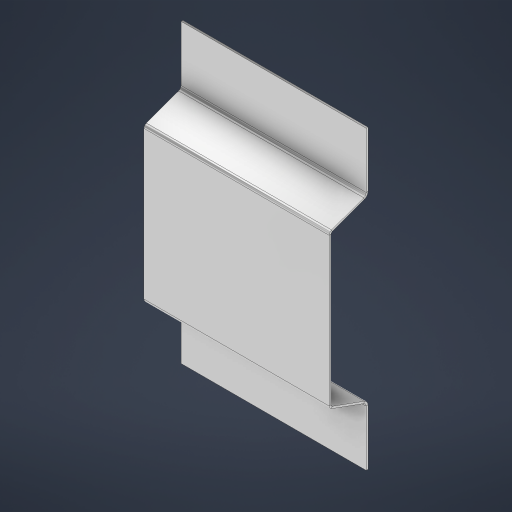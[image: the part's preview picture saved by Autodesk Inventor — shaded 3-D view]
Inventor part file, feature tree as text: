
AUTODESK INVENTOR PART (.ipt)
format: ipt  version: 2024.3 (Build 283343010, 343A)  size: 211,456 bytes
history: native  units: mm
features: other x4, sketch x2
ambient origin geometry x8: Origin, YZ Plane, XZ Plane, XY Plane, X Axis, Y Axis, Z Axis, Center Point
bodies: Volumenkörper1 (feature_tree)
feature tree (6):
  sketch  "Skizze1"  dims[d0=0.1mm]
  other  "Konturlasche1"
  sketch  "Skizze2"  dims[d1=10.0mm d2=2.0mm d3=10.0mm d4=3.0mm d5=0.2mm d6=0.1mm d7=0.1mm d8=0.05mm d9=0.2mm d10=0.1mm d11=10.0mm d12=0.1mm d13=0.5mm d14=0.4mm d15=0.1mm d16=0.1mm d17=12.217305mm]
  other  "Grobblech1"
  other  "Biegung1"
  other  "Ecke1"
